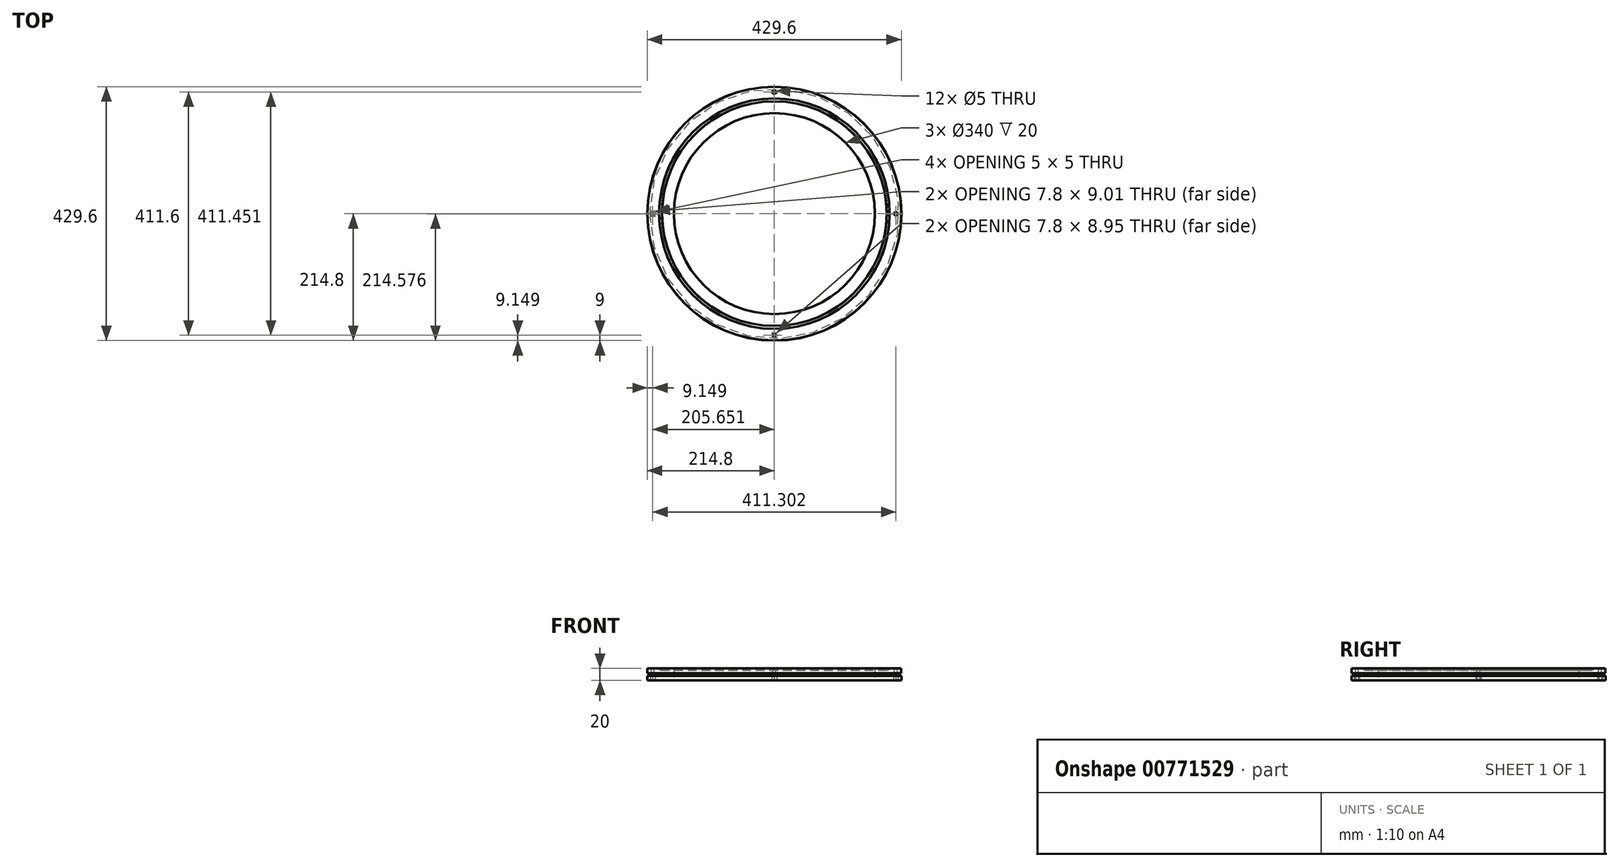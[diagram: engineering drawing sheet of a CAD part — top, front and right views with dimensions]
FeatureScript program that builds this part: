
annotation { "Feature Type Name" : "Feature", "Feature Type Description" : "" }
export const myFeature = defineFeature(function(context is Context, id is Id, definition is map)
    precondition{}
    {
        {
            var Q0;
            Q0=qCreatedBy(makeId("Front.planeOp"),FACE);
            var sketch = newSketch(context, id + "F0", { "sketchPlane" : qUnion([Q0])});
            skLineSegment(sketch, "E0", {"start": v(170, 20) * mm, "end": v(170, 0) * mm});
            skLineSegment(sketch, "E1", {"start": v(170, 0) * mm, "end": v(214.8, 0) * mm});
            skLineSegment(sketch, "E2", {"start": v(214.65, 20) * mm, "end": v(214.65, 12.29) * mm});
            skLineSegment(sketch, "E3", {"start": v(214.8, 0) * mm, "end": v(214.8, 7.71) * mm});
            skArc(sketch, "E4", {"start": v(214.65, 12.29) * mm, "mid": v(211.22, 9.89) * mm, "end": v(214.8, 7.71) * mm});
            skLineSegment(sketch, "E5", {"start": v(0, 0) * mm, "end": v(0, 70.95) * mm});
            skLineSegment(sketch, "E6", {"start": v(170, 20) * mm, "end": v(190, 20) * mm});
            skLineSegment(sketch, "E7", {"start": v(214.65, 20) * mm, "end": v(195, 20) * mm});
            skArc(sketch, "E8", {"start": v(190, 20) * mm, "mid": v(192.5, 17.37) * mm, "end": v(195, 20) * mm});
            skSolve(sketch);
        }
        {
            var Q0;
            Q0 = qSketchRegion(id + "F0", true);
            var Q1;
            Q1=sQuery(id+"F0.wireOp",EDGE,"E5");
            revolve(context, id + "F1", {"surfaceOperationType" : NewSurfaceOperationType.NEW, "entities" : qUnion([Q0]), "axis" : qUnion([Q1]), "revolveType" : RevolveType.FULL});
        }
        {
            var Q0;
            Q0=makeQuery(id+"F1.opRevolve","SWEPT_FACE",FACE,{"disambiguationData":[OSD([sQuery(id+"F0.wireOp",EDGE,"E7")])]});
            var sketch = newSketch(context, id + "F2", { "sketchPlane" : qUnion([Q0])});
            skCircle(sketch, "E9", {"center": v(205.65, 0) * mm, "radius": 2.5 * mm});
            skCircle(sketch, "E10", {"center": v(0, 205.8) * mm, "radius": 2.5 * mm});
            skCircle(sketch, "E11", {"center": v(-205.65, 0) * mm, "radius": 2.5 * mm});
            skCircle(sketch, "E12", {"center": v(0, -205.65) * mm, "radius": 2.5 * mm});
            skSolve(sketch);
        }
        {
            var Q0;
            Q0 = qSketchRegion(id + "F2", true);
            extrude(context, id + "F3", {"entities" : qUnion([Q0]), "operationType" : NewBodyOperationType.REMOVE, "endBound" : BoundingType.THROUGH_ALL, "oppositeDirection" : true, "depth" : 25 * mm, "offsetDistance" : 25 * mm});
        }
        {
            var Q0;
            Q0=makeQuery(id+"F1.opRevolve","SWEPT_FACE",FACE,{"disambiguationData":[OSD([sQuery(id+"F0.wireOp",EDGE,"E1")])]});
            var sketch = newSketch(context, id + "F4", { "sketchPlane" : qUnion([Q0])});
            skLineSegment(sketch, "E13", {"start": v(209.55, 2.48) * mm, "end": v(205.65, 4.73) * mm});
            skLineSegment(sketch, "E14", {"start": v(205.65, 4.73) * mm, "end": v(201.75, 2.48) * mm});
            skLineSegment(sketch, "E15", {"start": v(201.75, 2.48) * mm, "end": v(201.75, -2.03) * mm});
            skLineSegment(sketch, "E16", {"start": v(201.75, -2.03) * mm, "end": v(205.65, -4.28) * mm});
            skLineSegment(sketch, "E17", {"start": v(205.65, -4.28) * mm, "end": v(209.55, -2.03) * mm});
            skLineSegment(sketch, "E18", {"start": v(209.55, -2.03) * mm, "end": v(209.55, 2.48) * mm});
            skPoint(sketch, "E19", {"position": v(205.65, 0) * mm});
            skLineSegment(sketch, "E20", {"start": v(0, 0) * mm, "end": v(0, 55.35) * mm});
            skPoint(sketch, "E21.MirrorP", {"position": v(-205.65, 0) * mm});
            skLineSegment(sketch, "E22.MirrorCS", {"start": v(-209.55, 2.48) * mm, "end": v(-205.65, 4.73) * mm});
            skLineSegment(sketch, "E23.MirrorCS", {"start": v(-205.65, 4.73) * mm, "end": v(-201.75, 2.48) * mm});
            skLineSegment(sketch, "E24.MirrorCS", {"start": v(-201.75, -2.03) * mm, "end": v(-205.65, -4.28) * mm});
            skLineSegment(sketch, "E25.MirrorCS", {"start": v(-209.55, -2.03) * mm, "end": v(-209.55, 2.48) * mm});
            skLineSegment(sketch, "E26.MirrorCS", {"start": v(-205.65, -4.28) * mm, "end": v(-209.55, -2.03) * mm});
            skLineSegment(sketch, "E27.MirrorCS", {"start": v(-201.75, 2.48) * mm, "end": v(-201.75, -2.03) * mm});
            skPoint(sketch, "E28", {"position": v(0, -205.8) * mm});
            skLineSegment(sketch, "E29", {"start": v(3.9, -203.52) * mm, "end": v(0, -201.33) * mm});
            skLineSegment(sketch, "E30", {"start": v(-3.9, -203.52) * mm, "end": v(-3.9, -208.08) * mm});
            skLineSegment(sketch, "E31", {"start": v(-3.9, -208.08) * mm, "end": v(0, -210.27) * mm});
            skLineSegment(sketch, "E32", {"start": v(3.9, -208.02) * mm, "end": v(3.9, -203.52) * mm});
            skLineSegment(sketch, "E33", {"start": v(-3.9, -203.52) * mm, "end": v(0, -201.33) * mm});
            skLineSegment(sketch, "E34", {"start": v(0, -210.27) * mm, "end": v(3.9, -208.02) * mm});
            skLineSegment(sketch, "E35", {"start": v(0, 0) * mm, "end": v(41.73, 0) * mm});
            skLineSegment(sketch, "E36.MirrorCS", {"start": v(0, 210.27) * mm, "end": v(3.9, 208.02) * mm});
            skLineSegment(sketch, "E37.MirrorCS", {"start": v(-3.9, 203.52) * mm, "end": v(0, 201.33) * mm});
            skLineSegment(sketch, "E38.MirrorCS", {"start": v(-3.9, 203.52) * mm, "end": v(-3.9, 208.08) * mm});
            skLineSegment(sketch, "E39.MirrorCS", {"start": v(3.9, 203.52) * mm, "end": v(0, 201.33) * mm});
            skLineSegment(sketch, "E40.MirrorCS", {"start": v(-3.9, 208.08) * mm, "end": v(0, 210.27) * mm});
            skLineSegment(sketch, "E41.MirrorCS", {"start": v(3.9, 208.02) * mm, "end": v(3.9, 203.52) * mm});
            skPoint(sketch, "E42.MirrorP", {"position": v(0, 205.8) * mm});
            skSolve(sketch);
        }
        {
            var Q0;
            Q0 = qSketchRegion(id + "F4", true);
            extrude(context, id + "F5", {"entities" : qUnion([Q0]), "operationType" : NewBodyOperationType.REMOVE, "oppositeDirection" : true, "depth" : 10 * mm, "offsetDistance" : 25 * mm});
        }
    });
